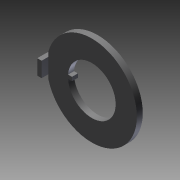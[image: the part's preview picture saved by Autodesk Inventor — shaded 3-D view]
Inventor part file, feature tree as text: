
AUTODESK INVENTOR PART (.ipt)
format: ipt  version: 2015 (Build 190159000, 159)  size: 107,520 bytes
history: native  units: in
note: dims shown in document units (in); Inventor stores cm internally (conversion verified against a paired STEP export)
features: other x7, extrude x2, sketch x2
ambient origin geometry x8: Origin, YZ Plane, XZ Plane, XY Plane, X Axis, Y Axis, Z Axis, Center Point
bodies: Solid1 (feature_tree)
feature tree (11):
  extrude  "Extrusion1"  Depth=0.079in TaperAngle=0.0deg
  extrude  "Extrusion2"  [1 undecoded]
  other  "ring_XY"
  other  "ring_YZ"
  other  "ring_ZX"
  other  "ring_X"
  other  "ring_Y"
  other  "ring_Z"
  other  "ring_Center"
  sketch  "Sketch_4"
  sketch  "Sketch_2"  dims[d0=0.031in d1=0.0in d2=0.079in d3=0.0in]
note: 1 required parameter value undecoded (feature->parameter linkage not recoverable at this tier; creation-order binding heuristic only, values carry confidence <= 0.55)
